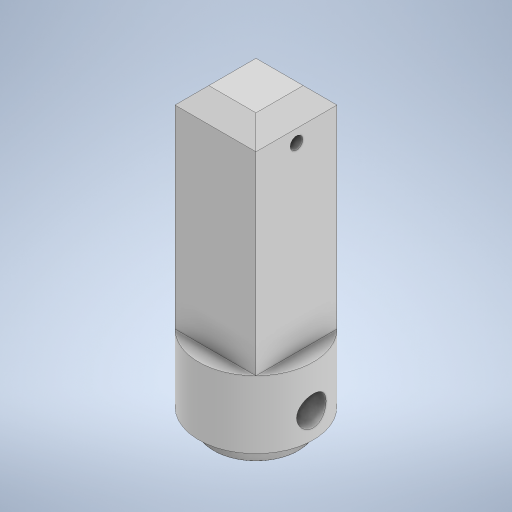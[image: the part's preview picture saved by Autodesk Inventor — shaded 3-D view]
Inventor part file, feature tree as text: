
AUTODESK INVENTOR PART (.ipt)
format: ipt  version: 2024.2 (Build 282272000, 272)  size: 296,960 bytes
history: native  units: mm
features: sketch x6, extrude x4, hole x2, fillet x1, chamfer x1
ambient origin geometry x8: Origin, YZ Plane, XZ Plane, XY Plane, X Axis, Y Axis, Z Axis, Center Point
bodies: Solid1 (feature_tree)
feature tree (14):
  extrude  "Extrusion1"  Depth=9.6mm
  extrude  "Extrusion5"  Depth=35.0mm
  hole  "Hole1"  [1 undecoded]
  extrude  "Extrusion7"  Depth=5.0mm
  hole  "Hole3"  [1 undecoded]
  extrude  "Extrusion8"  Depth=10.0mm
  fillet  "Fillet3"  Radius=2.0mm
  chamfer  "Chamfer1"  Distance=2.0mm
  sketch  "Sketch1"  dims[d0=9.6mm d1=9.6mm]
  sketch  "Sketch5"  dims[d2=35.0mm d3=0.0mm d14=4.2mm]
  sketch  "Sketch6"  dims[d15=10.0mm d16=0.0mm d18=3.5mm]
  sketch  "Sketch9"  dims[d19=1.5mm d20=6.0mm d21=4.0mm d22=2.0mm d23=90.0deg d24=8.0mm d25=20.594885mm d41=5.0mm]
  sketch  "Sketch10"  dims[d42=3.5mm d43=5.0mm d44=4.0mm d45=0.0mm d46=0.0mm]
  sketch  "Sketch11"  dims[d47=4.0mm d48=6.0mm d49=4.0mm d50=2.0mm d51=90.0deg d52=9.0mm d53=20.594885mm d55=10.0mm d56=2.0mm d57=0.0mm d58=2.0mm d60=2.0mm d61=2.0mm d62=45.0deg d63=15.0mm]
note: 2 required parameter values undecoded (feature->parameter linkage not recoverable at this tier; creation-order binding heuristic only, values carry confidence <= 0.55)
